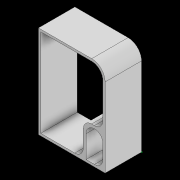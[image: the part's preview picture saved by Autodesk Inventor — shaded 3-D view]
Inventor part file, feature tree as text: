
AUTODESK INVENTOR PART (.ipt)
format: ipt  version: 2022 (Build 260153000, 153)  size: 125,952 bytes
history: native  units: in
note: dims shown in document units (in); Inventor stores cm internally (conversion verified against a paired STEP export)
features: sketch x3, extrude x2, fillet x2, shell x1
ambient origin geometry x8: Origin, YZ Plane, XZ Plane, XY Plane, X Axis, Y Axis, Z Axis, Center Point
bodies: Solid1 (feature_tree)
feature tree (8):
  extrude  "Extrusion1"  Depth=2.5591in
  shell  "Shell1"  Thickness=6.4961in
  fillet  "Fillet1"  Radius=2.5591in
  extrude  "Extrusion4"  Depth=0.5906in
  fillet  "Fillet3"  Radius=0.1969in
  sketch  "Sketch4"  dims[d23=0.1969in d24=1.1811in d25=2.1654in d26=2.5591in d27=0.0in d28=0.5906in]
  sketch  "Sketch1"  dims[d0=0.9449in d1=3.7402in d2=6.4961in d3=2.5591in d4=0.0in]
  sketch  "Sketch3"  dims[d5=0.1575in d13=0.5906in d22=0.1969in]
